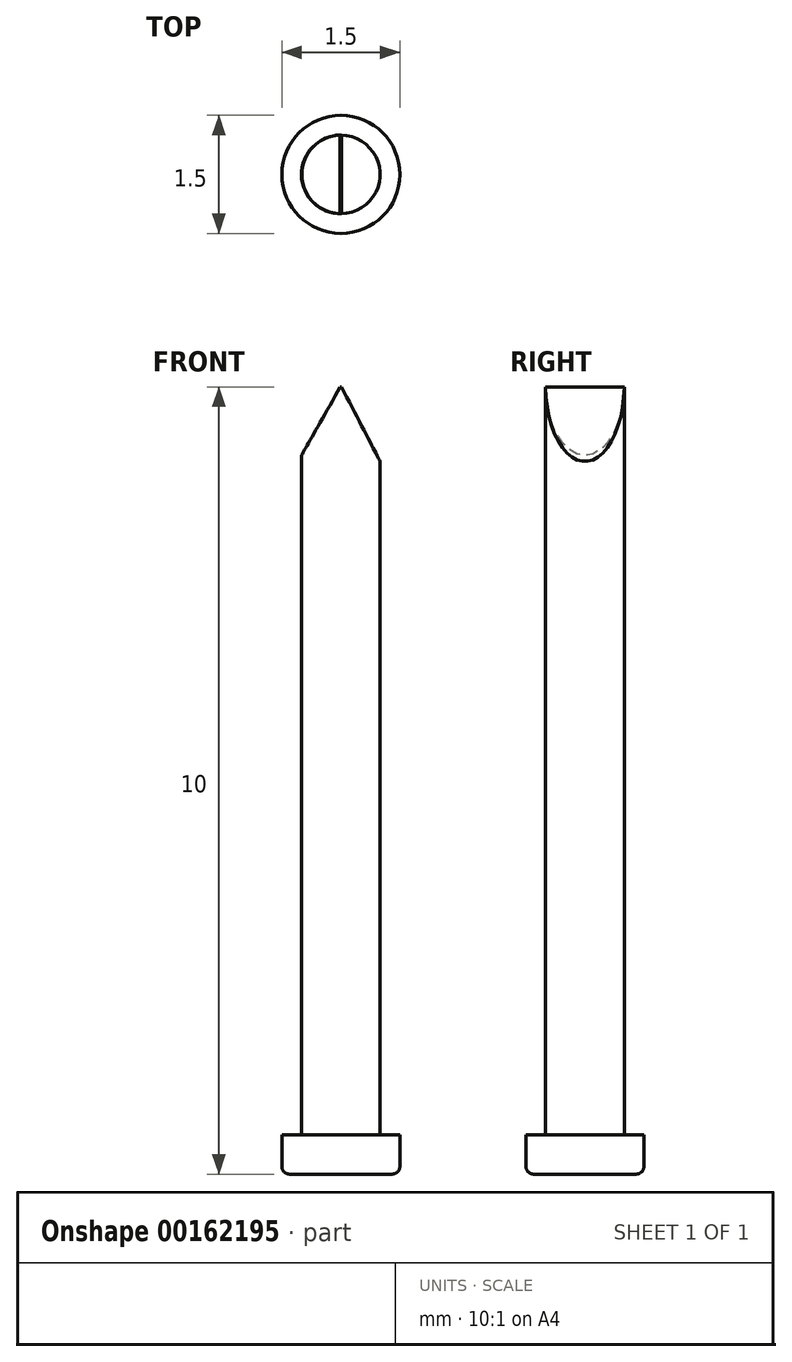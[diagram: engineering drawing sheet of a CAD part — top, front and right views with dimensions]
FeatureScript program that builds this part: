
annotation { "Feature Type Name" : "Feature", "Feature Type Description" : "" }
export const myFeature = defineFeature(function(context is Context, id is Id, definition is map)
    precondition{}
    {
        {
            var Q0;
            Q0=qCreatedBy(makeId("Top.planeOp"),FACE);
            var sketch = newSketch(context, id + "F0", { "sketchPlane" : qUnion([Q0])});
            skCircle(sketch, "E0", {"center": v(0, 0) * mm, "radius": 0.5 * mm});
            skCircle(sketch, "E1", {"center": v(0, 0) * mm, "radius": 0.75 * mm});
            skSolve(sketch);
        }
        {
            var Q0;
            Q0=makeQuery(id+"F0.imprint","IMPRINT",FACE,{"disambiguationData":[TD([[makeQuery(id+"F0.imprint","IMPRINT",EDGE,{"derivedFrom":sQuery(id+"F0.wireOp",EDGE,"E0")}),1.0]])]});
            extrude(context, id + "F1", {"entities" : qUnion([Q0]), "depth" : 10 * mm});
        }
        {
            var Q0;
            Q0=makeQuery(id+"F0.imprint","IMPRINT",FACE,{"disambiguationData":[TD([[makeQuery(id+"F0.imprint","IMPRINT",EDGE,{"derivedFrom":sQuery(id+"F0.wireOp",EDGE,"E0")}),-1.0]])]});
            extrude(context, id + "F2", {"entities" : qUnion([Q0]), "operationType" : NewBodyOperationType.ADD, "depth" : 0.5 * mm});
        }
        {
            var Q0;
            Q0=makeQuery(id+"F2.opExtrude","CAP_EDGE",EDGE,{"disambiguationData":[OSD([sQuery(id+"F0.wireOp",EDGE,"E1")])],"isStart":true});
            fillet(context, id + "F3", {"entities" : qUnion([Q0]), "radius" : 0.1 * mm, "tangentPropagation" : true, "allowEdgeOverflow" : false});
        }
        {
            var Q0;
            Q0=qCreatedBy(makeId("Front.planeOp"),FACE);
            var sketch = newSketch(context, id + "F4", { "sketchPlane" : qUnion([Q0])});
            skLineSegment(sketch, "E2", {"start": v(0, 10.01) * mm, "end": v(0.63, 8.8) * mm});
            skLineSegment(sketch, "E3", {"start": v(0, 10.01) * mm, "end": v(-0.7, 8.8) * mm});
            skLineSegment(sketch, "E4", {"start": v(0.63, 8.8) * mm, "end": v(0.63, 10.81) * mm});
            skLineSegment(sketch, "E5", {"start": v(0.63, 10.81) * mm, "end": v(-0.74, 10.81) * mm});
            skLineSegment(sketch, "E6", {"start": v(-0.74, 10.81) * mm, "end": v(-0.74, 8.8) * mm});
            skLineSegment(sketch, "E7", {"start": v(-0.74, 8.8) * mm, "end": v(-0.7, 8.8) * mm});
            skSolve(sketch);
        }
        {
            var Q0;
            Q0=makeQuery(id+"F4.imprint","IMPRINT",FACE,{"disambiguationData":[TD([[makeQuery(id+"F4.imprint","IMPRINT",EDGE,{"derivedFrom":sQuery(id+"F4.wireOp",EDGE,"E2")}),1.0]])]});
            extrude(context, id + "F5", {"entities" : qUnion([Q0]), "operationType" : NewBodyOperationType.REMOVE, "oppositeDirection" : true, "depth" : 25 * mm, "hasSecondDirection" : true, "secondDirectionOppositeDirection" : false, "secondDirectionDepth" : 25 * mm});
        }
    });
